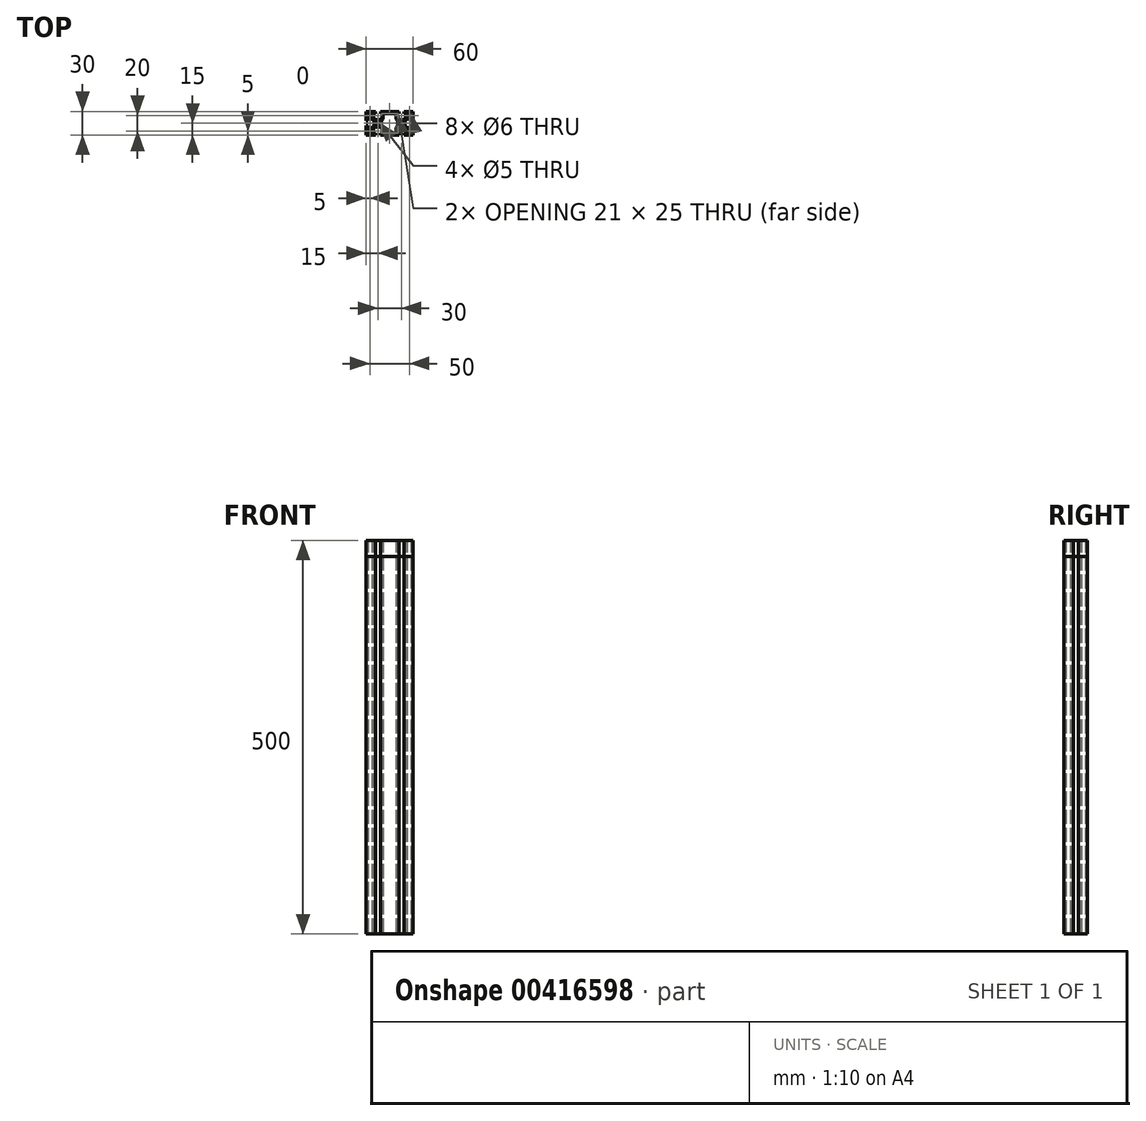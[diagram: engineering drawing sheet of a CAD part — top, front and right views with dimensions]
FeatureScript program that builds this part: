
annotation { "Feature Type Name" : "Feature", "Feature Type Description" : "" }
export const myFeature = defineFeature(function(context is Context, id is Id, definition is map)
    precondition{}
    {
        {
            var Q0;
            Q0=qCreatedBy(makeId("Top.planeOp"),FACE);
            var sketch = newSketch(context, id + "F0", { "sketchPlane" : qUnion([Q0])});
            skCircle(sketch, "E0", {"center": v(0, 0) * mm, "radius": 2.5 * mm});
            skLineSegment(sketch, "E1", {"start": v(0, 0) * mm, "end": v(-15, 0) * mm, "construction": true});
            skLineSegment(sketch, "E2", {"start": v(-15, 0) * mm, "end": v(-15, 15) * mm, "construction": true});
            skLineSegment(sketch, "E3", {"start": v(-15, 15) * mm, "end": v(0, 15) * mm, "construction": true});
            skLineSegment(sketch, "E4", {"start": v(0, 15) * mm, "end": v(0, 0) * mm, "construction": true});
            skLineSegment(sketch, "E5", {"start": v(-15, 15) * mm, "end": v(0, 0) * mm, "construction": true});
            skLineSegment(sketch, "E6", {"start": v(-15, 10) * mm, "end": v(-10, 10) * mm, "construction": true});
            skPoint(sketch, "E7", {"position": v(-15, 3.15) * mm});
            skPoint(sketch, "E8", {"position": v(-15, 5.5) * mm});
            skCircle(sketch, "E9", {"center": v(-10, 10) * mm, "radius": 3 * mm});
            skLineSegment(sketch, "E10", {"start": v(-15, 15) * mm, "end": v(-15, 3.15) * mm});
            skLineSegment(sketch, "E11", {"start": v(-15, 3.15) * mm, "end": v(-12.5, 3.15) * mm});
            skLineSegment(sketch, "E12", {"start": v(-12.5, 3.15) * mm, "end": v(-12.5, 5.5) * mm});
            skPoint(sketch, "E13", {"position": v(-4.5, 0) * mm});
            skLineSegment(sketch, "E14", {"start": v(-12.5, 5.5) * mm, "end": v(-5.5, 5.5) * mm, "construction": true});
            skArc(sketch, "E15", {"start": v(-4.5, 0) * mm, "mid": v(-5.13, 3) * mm, "end": v(-6.9, 5.5) * mm});
            skLineSegment(sketch, "E16", {"start": v(-12.5, 5.5) * mm, "end": v(-6.9, 5.5) * mm});
            skLineSegment(sketch, "E17.0.MirrorCS", {"start": v(-15, 15) * mm, "end": v(-3.15, 15) * mm});
            skPoint(sketch, "E18.visualSharp", {"position": v(-15, 15) * mm});
            skLineSegment(sketch, "E18.filletArc", {"start": v(-15, 15) * mm, "end": v(-15, 15) * mm});
            skLineSegment(sketch, "E19.0.MirrorCS", {"start": v(-3.15, 15) * mm, "end": v(-3.15, 12.5) * mm});
            skLineSegment(sketch, "E20.0.MirrorCS", {"start": v(-3.15, 12.5) * mm, "end": v(-5.5, 12.5) * mm});
            skLineSegment(sketch, "E21.0.MirrorCS", {"start": v(-5.5, 12.5) * mm, "end": v(-5.5, 6.9) * mm});
            skArc(sketch, "E22.0.MirrorCS", {"start": v(0, 4.5) * mm, "mid": v(-3, 5.13) * mm, "end": v(-5.5, 6.9) * mm});
            skArc(sketch, "E23.0.MirrorCS", {"start": v(-4.5, 0) * mm, "mid": v(-5.13, -3) * mm, "end": v(-6.9, -5.5) * mm});
            skLineSegment(sketch, "E24.0.MirrorCS", {"start": v(-12.5, -5.5) * mm, "end": v(-6.9, -5.5) * mm});
            skLineSegment(sketch, "E25.0.MirrorCS", {"start": v(-12.5, -3.15) * mm, "end": v(-12.5, -5.5) * mm});
            skLineSegment(sketch, "E26.0.MirrorCS", {"start": v(-15, -3.15) * mm, "end": v(-12.5, -3.15) * mm});
            skLineSegment(sketch, "E27.0.MirrorCS", {"start": v(-15, -15) * mm, "end": v(-15, -3.15) * mm});
            skLineSegment(sketch, "E28.0.MirrorCS", {"start": v(-15, -15) * mm, "end": v(-15, -15) * mm});
            skLineSegment(sketch, "E29.0.MirrorCS", {"start": v(-15, -15) * mm, "end": v(-3.15, -15) * mm});
            skLineSegment(sketch, "E30.0.MirrorCS", {"start": v(-3.15, -15) * mm, "end": v(-3.15, -12.5) * mm});
            skLineSegment(sketch, "E31.0.MirrorCS", {"start": v(-3.15, -12.5) * mm, "end": v(-5.5, -12.5) * mm});
            skLineSegment(sketch, "E32.0.MirrorCS", {"start": v(-5.5, -12.5) * mm, "end": v(-5.5, -6.9) * mm});
            skArc(sketch, "E33.0.MirrorCS", {"start": v(0, -4.5) * mm, "mid": v(-3, -5.13) * mm, "end": v(-5.5, -6.9) * mm});
            skCircle(sketch, "E34.0.MirrorC", {"center": v(-10, -10) * mm, "radius": 3 * mm});
            skArc(sketch, "E35.0.MirrorCS", {"start": v(0, 4.5) * mm, "mid": v(3, 5.13) * mm, "end": v(5.5, 6.9) * mm});
            skLineSegment(sketch, "E36.0.MirrorCS", {"start": v(5.5, 12.5) * mm, "end": v(5.5, 6.9) * mm});
            skLineSegment(sketch, "E37.0.MirrorCS", {"start": v(3.15, 12.5) * mm, "end": v(5.5, 12.5) * mm});
            skLineSegment(sketch, "E38.0.MirrorCS", {"start": v(3.15, 15) * mm, "end": v(3.15, 12.5) * mm});
            skArc(sketch, "E39.0.MirrorCS", {"start": v(0, -4.5) * mm, "mid": v(3, -5.13) * mm, "end": v(5.5, -6.9) * mm});
            skLineSegment(sketch, "E40.0.MirrorCS", {"start": v(5.5, -12.5) * mm, "end": v(5.5, -6.9) * mm});
            skLineSegment(sketch, "E41.0.MirrorCS", {"start": v(3.15, -12.5) * mm, "end": v(5.5, -12.5) * mm});
            skLineSegment(sketch, "E42.0.MirrorCS", {"start": v(3.15, -15) * mm, "end": v(3.15, -12.5) * mm});
            skLineSegment(sketch, "E43", {"start": v(0, 0) * mm, "end": v(30, 0) * mm, "construction": true});
            skPoint(sketch, "E44", {"position": v(15, 0) * mm});
            skLineSegment(sketch, "E45", {"start": v(15, 15) * mm, "end": v(15, -15) * mm, "construction": true});
            skCircle(sketch, "E46.0.MirrorC", {"center": v(30, 0) * mm, "radius": 2.5 * mm});
            skLineSegment(sketch, "E47.0.MirrorCS", {"start": v(26.85, 15) * mm, "end": v(26.85, 12.5) * mm});
            skLineSegment(sketch, "E48.0.MirrorCS", {"start": v(26.85, 12.5) * mm, "end": v(24.5, 12.5) * mm});
            skLineSegment(sketch, "E49.0.MirrorCS", {"start": v(24.5, 12.5) * mm, "end": v(24.5, 6.9) * mm});
            skArc(sketch, "E50.0.MirrorCS", {"start": v(30, 4.5) * mm, "mid": v(27, 5.13) * mm, "end": v(24.5, 6.9) * mm});
            skArc(sketch, "E51.0.MirrorCS", {"start": v(30, 4.5) * mm, "mid": v(33, 5.13) * mm, "end": v(35.5, 6.9) * mm});
            skLineSegment(sketch, "E52.0.MirrorCS", {"start": v(35.5, 12.5) * mm, "end": v(35.5, 6.9) * mm});
            skLineSegment(sketch, "E53.0.MirrorCS", {"start": v(33.15, 12.5) * mm, "end": v(35.5, 12.5) * mm});
            skLineSegment(sketch, "E54.0.MirrorCS", {"start": v(33.15, 15) * mm, "end": v(33.15, 12.5) * mm});
            skLineSegment(sketch, "E55.0.MirrorCS", {"start": v(45, 15) * mm, "end": v(33.15, 15) * mm});
            skLineSegment(sketch, "E56.0.MirrorCS", {"start": v(45, 15) * mm, "end": v(45, 15) * mm});
            skLineSegment(sketch, "E57.0.MirrorCS", {"start": v(45, 15) * mm, "end": v(45, 3.15) * mm});
            skLineSegment(sketch, "E58.0.MirrorCS", {"start": v(45, 3.15) * mm, "end": v(42.5, 3.15) * mm});
            skLineSegment(sketch, "E59.0.MirrorCS", {"start": v(42.5, 3.15) * mm, "end": v(42.5, 5.5) * mm});
            skLineSegment(sketch, "E60.0.MirrorCS", {"start": v(42.5, 5.5) * mm, "end": v(36.9, 5.5) * mm});
            skArc(sketch, "E61.0.MirrorCS", {"start": v(34.5, 0) * mm, "mid": v(35.13, 3) * mm, "end": v(36.9, 5.5) * mm});
            skArc(sketch, "E62.0.MirrorCS", {"start": v(34.5, 0) * mm, "mid": v(35.13, -3) * mm, "end": v(36.9, -5.5) * mm});
            skLineSegment(sketch, "E63.0.MirrorCS", {"start": v(42.5, -5.5) * mm, "end": v(36.9, -5.5) * mm});
            skLineSegment(sketch, "E64.0.MirrorCS", {"start": v(42.5, -3.15) * mm, "end": v(42.5, -5.5) * mm});
            skLineSegment(sketch, "E65.0.MirrorCS", {"start": v(45, -3.15) * mm, "end": v(42.5, -3.15) * mm});
            skLineSegment(sketch, "E66.0.MirrorCS", {"start": v(45, -15) * mm, "end": v(45, -3.15) * mm});
            skLineSegment(sketch, "E67.0.MirrorCS", {"start": v(45, -15) * mm, "end": v(45, -15) * mm});
            skLineSegment(sketch, "E68.0.MirrorCS", {"start": v(45, -15) * mm, "end": v(33.15, -15) * mm});
            skLineSegment(sketch, "E69.0.MirrorCS", {"start": v(33.15, -15) * mm, "end": v(33.15, -12.5) * mm});
            skLineSegment(sketch, "E70.0.MirrorCS", {"start": v(33.15, -12.5) * mm, "end": v(35.5, -12.5) * mm});
            skLineSegment(sketch, "E71.0.MirrorCS", {"start": v(35.5, -12.5) * mm, "end": v(35.5, -6.9) * mm});
            skArc(sketch, "E72.0.MirrorCS", {"start": v(30, -4.5) * mm, "mid": v(33, -5.13) * mm, "end": v(35.5, -6.9) * mm});
            skArc(sketch, "E73.0.MirrorCS", {"start": v(30, -4.5) * mm, "mid": v(27, -5.13) * mm, "end": v(24.5, -6.9) * mm});
            skLineSegment(sketch, "E74.0.MirrorCS", {"start": v(24.5, -12.5) * mm, "end": v(24.5, -6.9) * mm});
            skLineSegment(sketch, "E75.0.MirrorCS", {"start": v(26.85, -12.5) * mm, "end": v(24.5, -12.5) * mm});
            skLineSegment(sketch, "E76.0.MirrorCS", {"start": v(26.85, -15) * mm, "end": v(26.85, -12.5) * mm});
            skCircle(sketch, "E77.0.MirrorC", {"center": v(40, -10) * mm, "radius": 3 * mm});
            skCircle(sketch, "E78.0.MirrorC", {"center": v(40, 10) * mm, "radius": 3 * mm});
            skLineSegment(sketch, "E79", {"start": v(3.15, 15) * mm, "end": v(26.85, 15) * mm});
            skLineSegment(sketch, "E80", {"start": v(3.15, -15) * mm, "end": v(26.85, -15) * mm});
            skLineSegment(sketch, "E81.0.MirrorCS", {"start": v(0, 15) * mm, "end": v(0, 30) * mm, "construction": true});
            skArc(sketch, "E82.0.MirrorCS", {"start": v(4.5, 0) * mm, "mid": v(5.05, 2.82) * mm, "end": v(6.62, 5.22) * mm});
            skLineSegment(sketch, "E83", {"start": v(6.9, 5.92) * mm, "end": v(6.9, 11.5) * mm});
            skLineSegment(sketch, "E84", {"start": v(7.9, 12.5) * mm, "end": v(15, 12.5) * mm});
            skPoint(sketch, "E85.visualSharp", {"position": v(6.9, 5.5) * mm});
            skArc(sketch, "E85.filletArc", {"start": v(6.62, 5.22) * mm, "mid": v(6.83, 5.54) * mm, "end": v(6.9, 5.92) * mm});
            skPoint(sketch, "E86.visualSharp", {"position": v(6.9, 12.5) * mm});
            skArc(sketch, "E86.filletArc", {"start": v(7.9, 12.5) * mm, "mid": v(7.2, 12.2) * mm, "end": v(6.9, 11.5) * mm});
            skPoint(sketch, "E87", {"position": v(15, 12.5) * mm});
            skLineSegment(sketch, "E88.0.MirrorCS", {"start": v(22.1, 12.5) * mm, "end": v(15, 12.5) * mm});
            skArc(sketch, "E89.0.MirrorCS", {"start": v(22.1, 12.5) * mm, "mid": v(22.8, 12.2) * mm, "end": v(23.1, 11.5) * mm});
            skLineSegment(sketch, "E90.0.MirrorCS", {"start": v(23.1, 5.92) * mm, "end": v(23.1, 11.5) * mm});
            skArc(sketch, "E91.0.MirrorCS", {"start": v(23.38, 5.22) * mm, "mid": v(23.17, 5.54) * mm, "end": v(23.1, 5.92) * mm});
            skArc(sketch, "E92.0.MirrorCS", {"start": v(25.5, 0) * mm, "mid": v(24.95, 2.82) * mm, "end": v(23.38, 5.22) * mm});
            skArc(sketch, "E93.0.MirrorCS", {"start": v(4.5, 0) * mm, "mid": v(5.05, -2.82) * mm, "end": v(6.62, -5.22) * mm});
            skPoint(sketch, "E94.0.MirrorP", {"position": v(6.9, -5.5) * mm});
            skArc(sketch, "E95.0.MirrorCS", {"start": v(6.62, -5.22) * mm, "mid": v(6.83, -5.54) * mm, "end": v(6.9, -5.92) * mm});
            skLineSegment(sketch, "E96.0.MirrorCS", {"start": v(6.9, -5.92) * mm, "end": v(6.9, -11.5) * mm});
            skLineSegment(sketch, "E97.0.MirrorCS", {"start": v(7.9, -12.5) * mm, "end": v(15, -12.5) * mm});
            skArc(sketch, "E98.0.MirrorCS", {"start": v(7.9, -12.5) * mm, "mid": v(7.2, -12.2) * mm, "end": v(6.9, -11.5) * mm});
            skLineSegment(sketch, "E99.0.MirrorCS", {"start": v(22.1, -12.5) * mm, "end": v(15, -12.5) * mm});
            skArc(sketch, "E100.0.MirrorCS", {"start": v(22.1, -12.5) * mm, "mid": v(22.8, -12.2) * mm, "end": v(23.1, -11.5) * mm});
            skLineSegment(sketch, "E101.0.MirrorCS", {"start": v(23.1, -5.92) * mm, "end": v(23.1, -11.5) * mm});
            skArc(sketch, "E102.0.MirrorCS", {"start": v(23.38, -5.22) * mm, "mid": v(23.17, -5.54) * mm, "end": v(23.1, -5.92) * mm});
            skArc(sketch, "E103.0.MirrorCS", {"start": v(25.5, 0) * mm, "mid": v(24.95, -2.82) * mm, "end": v(23.38, -5.22) * mm});
            skSolve(sketch);
        }
        {
            var Q0;
            Q0=qSketchRegion(id+"F0",true);
            extrude(context, id + "F1", {"entities" : qUnion([Q0]), "depth" : 500 * mm});
        }
        {
            var Q0;
            Q0=qSketchRegion(id+"F0",true);
            extrude(context, id + "F2", {"entities" : qUnion([Q0]), "depth" : 480 * mm});
        }
    });
